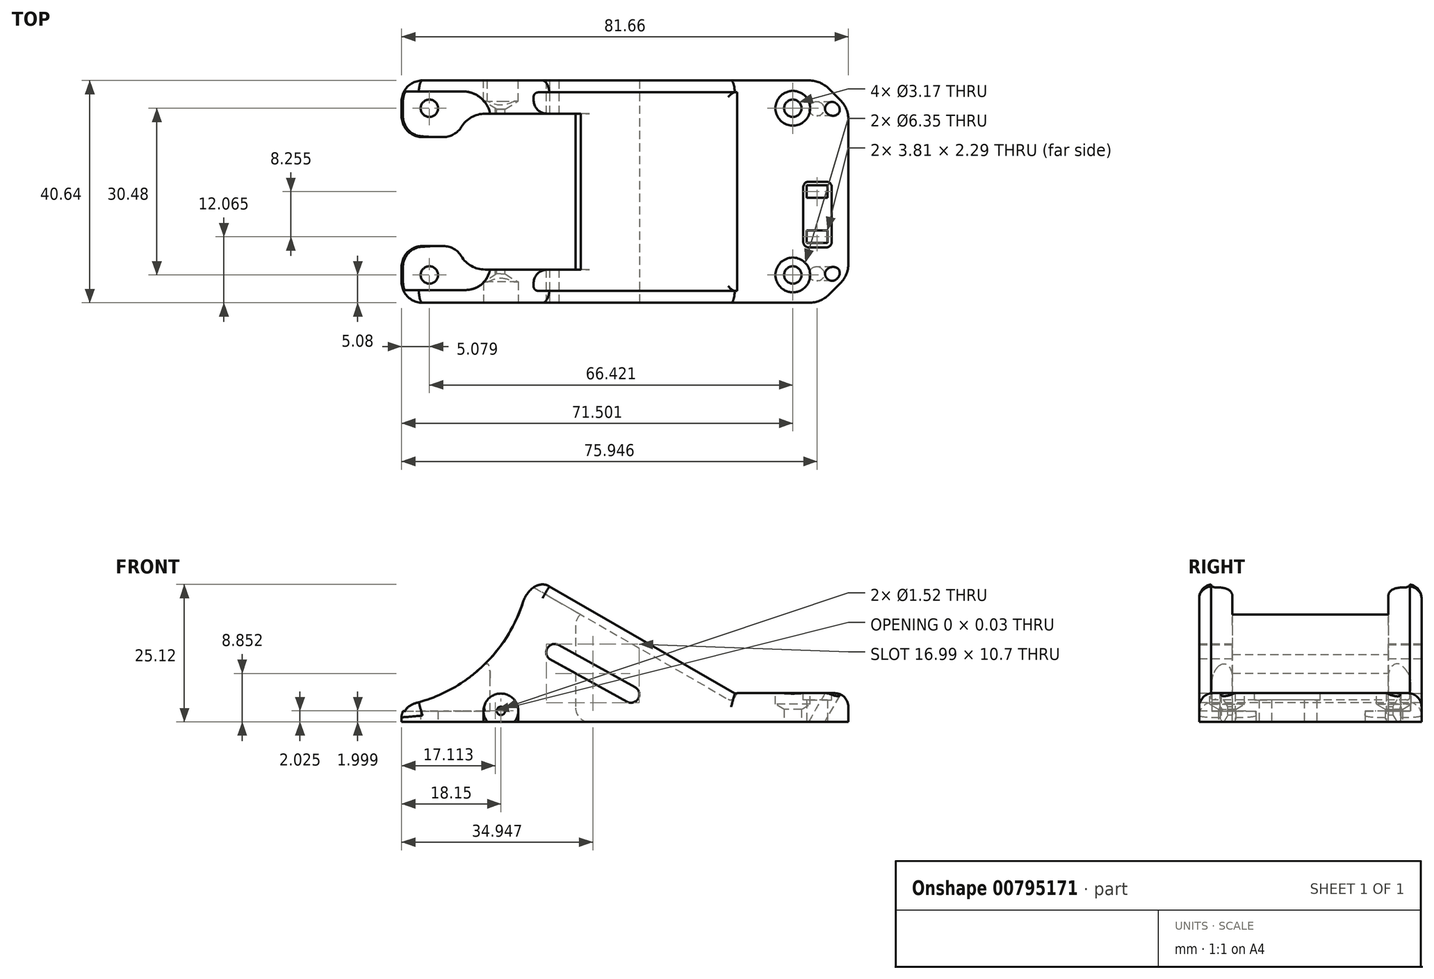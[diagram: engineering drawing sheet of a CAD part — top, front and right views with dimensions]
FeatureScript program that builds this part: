
annotation { "Feature Type Name" : "Feature", "Feature Type Description" : "" }
export const myFeature = defineFeature(function(context is Context, id is Id, definition is map)
    precondition{}
    {
        {
            var Q0;
            Q0=qCreatedBy(makeId("Top.planeOp"),FACE);
            var sketch = newSketch(context, id + "F0", { "sketchPlane" : qUnion([Q0])});
            skPoint(sketch, "E0.middle", {"position": v(0, 0) * mm});
            skCircle(sketch, "E1", {"center": v(-33.21, 15.24) * mm, "radius": 1.59 * mm});
            skCircle(sketch, "E2", {"center": v(-33.21, -15.24) * mm, "radius": 1.59 * mm});
            skCircle(sketch, "E3", {"center": v(33.21, 15.24) * mm, "radius": 1.59 * mm});
            skCircle(sketch, "E4", {"center": v(33.21, -15.24) * mm, "radius": 1.59 * mm});
            skLineSegment(sketch, "E5.bottom", {"start": v(-38.3, 20.32) * mm, "end": v(43.37, 20.32) * mm});
            skLineSegment(sketch, "E5.top", {"start": v(-38.3, -20.32) * mm, "end": v(43.37, -20.32) * mm});
            skLineSegment(sketch, "E5.left", {"start": v(-38.3, 20.32) * mm, "end": v(-38.3, 9.98) * mm});
            skLineSegment(sketch, "E5.right", {"start": v(43.37, 20.32) * mm, "end": v(43.37, -20.32) * mm});
            skLineSegment(sketch, "E6.bottom", {"start": v(-38.3, 9.98) * mm, "end": v(-26.81, 9.98) * mm});
            skLineSegment(sketch, "E6.top", {"start": v(-38.3, -9.96) * mm, "end": v(-26.82, -9.96) * mm});
            skLineSegment(sketch, "E7.left", {"start": v(-26.82, 14.25) * mm, "end": v(-26.82, 9.98) * mm});
            skLineSegment(sketch, "E7.right", {"start": v(-6.5, 14.25) * mm, "end": v(-6.5, -14.25) * mm});
            skLineSegment(sketch, "E8.trimOffspring", {"start": v(-38.3, -9.96) * mm, "end": v(-38.3, -20.32) * mm});
            skLineSegment(sketch, "E9.trimOffspring", {"start": v(-26.82, -9.96) * mm, "end": v(-26.82, -14.25) * mm});
            skLineSegment(sketch, "E10.trimOffspring", {"start": v(-26.82, 14.25) * mm, "end": v(-6.5, 14.25) * mm});
            skLineSegment(sketch, "E11.trimOffspring", {"start": v(-26.82, -14.25) * mm, "end": v(-6.5, -14.25) * mm});
            skLineSegment(sketch, "E12.bottom", {"start": v(39.56, -1.14) * mm, "end": v(35.75, -1.14) * mm});
            skLineSegment(sketch, "E12.top", {"start": v(39.56, 1.14) * mm, "end": v(35.75, 1.14) * mm});
            skLineSegment(sketch, "E12.left", {"start": v(39.56, -1.14) * mm, "end": v(39.56, 1.14) * mm});
            skLineSegment(sketch, "E12.right", {"start": v(35.75, -1.14) * mm, "end": v(35.75, 1.14) * mm});
            skPoint(sketch, "E12.middle", {"position": v(37.66, 0) * mm});
            skLineSegment(sketch, "E13.bottom", {"start": v(35.75, -7.11) * mm, "end": v(39.56, -7.11) * mm});
            skLineSegment(sketch, "E13.top", {"start": v(35.75, -9.4) * mm, "end": v(39.56, -9.4) * mm});
            skLineSegment(sketch, "E13.left", {"start": v(35.75, -7.11) * mm, "end": v(35.75, -9.4) * mm});
            skLineSegment(sketch, "E13.right", {"start": v(39.56, -7.11) * mm, "end": v(39.56, -9.4) * mm});
            skSolve(sketch);
        }
        {
            var Q0;
            Q0=makeQuery(id+"F0.imprint","IMPRINT",FACE,{"disambiguationData":[TD([[makeQuery(id+"F0.imprint","IMPRINT",EDGE,{"derivedFrom":sQuery(id+"F0.wireOp",EDGE,"E1")}),-1.0]])]});
            extrude(context, id + "F1", {"entities" : qUnion([Q0]), "depth" : 25.4 * mm, "offsetDistance" : 25.4 * mm});
        }
        {
            var Q0;
            Q0=qCreatedBy(makeId("Front.planeOp"),FACE);
            var sketch = newSketch(context, id + "F2", { "sketchPlane" : qUnion([Q0])});
            skLineSegment(sketch, "E14", {"start": v(-55.93, 50.59) * mm, "end": v(22.6, 5.24) * mm});
            skLineSegment(sketch, "E15", {"start": v(22.6, 5.24) * mm, "end": v(58.36, 5.24) * mm});
            skLineSegment(sketch, "E16", {"start": v(58.36, 5.24) * mm, "end": v(58.36, 49.59) * mm});
            skLineSegment(sketch, "E17", {"start": v(58.36, 49.59) * mm, "end": v(-55.93, 50.59) * mm});
            skSolve(sketch);
        }
        {
            var Q0;
            Q0 = qSketchRegion(id + "F2", true);
            extrude(context, id + "F3", {"entities" : qUnion([Q0]), "operationType" : NewBodyOperationType.REMOVE, "endBound" : BoundingType.SYMMETRIC, "oppositeDirection" : true, "depth" : 50.8 * mm, "offsetDistance" : 25.4 * mm});
        }
        {
            var Q0;
            Q0=qCreatedBy(makeId("Front.planeOp"),FACE);
            var sketch = newSketch(context, id + "F4", { "sketchPlane" : qUnion([Q0])});
            skCircle(sketch, "E18", {"center": v(-20.14, 2) * mm, "radius": 0.76 * mm});
            skSolve(sketch);
        }
        {
            var Q0;
            Q0 = qSketchRegion(id + "F4", true);
            extrude(context, id + "F5", {"entities" : qUnion([Q0]), "operationType" : NewBodyOperationType.REMOVE, "endBound" : BoundingType.SYMMETRIC, "depth" : 76.2 * mm, "offsetDistance" : 25.4 * mm});
        }
        {
            var Q0;
            Q0=qCreatedBy(makeId("Front.planeOp"),FACE);
            var sketch = newSketch(context, id + "F6", { "sketchPlane" : qUnion([Q0])});
            skCircle(sketch, "E19", {"center": v(-42.57, 30.4) * mm, "radius": 27.81 * mm});
            skSolve(sketch);
        }
        {
            var Q0;
            Q0=makeQuery(id+"F6.imprint","IMPRINT",FACE,{"disambiguationData":[TD([[makeQuery(id+"F6.imprint","IMPRINT",EDGE,{"derivedFrom":sQuery(id+"F6.wireOp",EDGE,"E19")}),1.0]])]});
            var Q1;
            Q1=sQuery(id+"F6.wireOp",EDGE,"E19");
            extrude(context, id + "F7", {"entities" : qUnion([Q0]), "operationType" : NewBodyOperationType.REMOVE, "surfaceEntities" : qUnion([Q1]), "endBound" : BoundingType.SYMMETRIC, "oppositeDirection" : true, "depth" : 76.2 * mm, "offsetDistance" : 25.4 * mm});
        }
        {
            var Q0;
            Q0=makeQuery(id+"F3.boolean.opBoolean","COPY",FACE,{"derivedFrom":makeQuery(id+"F3.opExtrude","SWEPT_FACE",FACE,{"disambiguationData":[OSD([sQuery(id+"F2.wireOp",EDGE,"E15")])]})});
            var sketch = newSketch(context, id + "F8", { "sketchPlane" : qUnion([Q0])});
            skPoint(sketch, "E20", {"position": v(33.21, -15.24) * mm});
            skPoint(sketch, "E21", {"position": v(33.21, 15.24) * mm});
            skPoint(sketch, "E22", {"position": v(-33.28, -15.24) * mm});
            skPoint(sketch, "E23", {"position": v(-33.28, 15.24) * mm});
            skSolve(sketch);
        }
        {
            var Q0;
            Q0=sQuery(id+"F8.wireOp",VERTEX,"E21");
            var Q1;
            Q1=sQuery(id+"F8.wireOp",VERTEX,"E20");
            var Q2;
            Q2=makeQuery(id+"F1.opExtrude","SWEPT_BODY",BODY,{"disambiguationData":[OSD([sQuery(id+"F0.wireOp",EDGE,"E1"),sQuery(id+"F0.wireOp",EDGE,"E2"),sQuery(id+"F0.wireOp",EDGE,"E3"),sQuery(id+"F0.wireOp",EDGE,"E4"),sQuery(id+"F0.wireOp",EDGE,"E5.bottom"),sQuery(id+"F0.wireOp",EDGE,"E5.top"),sQuery(id+"F0.wireOp",EDGE,"E5.left"),sQuery(id+"F0.wireOp",EDGE,"E5.right"),sQuery(id+"F0.wireOp",EDGE,"E6.bottom"),sQuery(id+"F0.wireOp",EDGE,"E6.top"),sQuery(id+"F0.wireOp",EDGE,"E7.left"),sQuery(id+"F0.wireOp",EDGE,"E7.right"),sQuery(id+"F0.wireOp",EDGE,"E8.trimOffspring"),sQuery(id+"F0.wireOp",EDGE,"E9.trimOffspring"),sQuery(id+"F0.wireOp",EDGE,"E10.trimOffspring"),sQuery(id+"F0.wireOp",EDGE,"E11.trimOffspring"),sQuery(id+"F0.wireOp",EDGE,"E12.bottom"),sQuery(id+"F0.wireOp",EDGE,"E12.top"),sQuery(id+"F0.wireOp",EDGE,"E12.left"),sQuery(id+"F0.wireOp",EDGE,"E12.right"),sQuery(id+"F0.wireOp",EDGE,"E13.bottom"),sQuery(id+"F0.wireOp",EDGE,"E13.top"),sQuery(id+"F0.wireOp",EDGE,"E13.left"),sQuery(id+"F0.wireOp",EDGE,"E13.right")])]});
            hole(context, id + "F9", {"style" : HoleStyle.SIMPLE, "endStyle" : HoleEndStyle.BLIND, "holeDiameter" : 6.35 * mm, "majorDiameter" : 6.35 * mm, "holeDepth" : 2.03 * mm, "isTappedThrough" : true, "tappedDepth" : 12.7 * mm, "tapClearance" : 3, "locations" : qUnion([Q0, Q1]), "scope" : qUnion([Q2])});
        }
        {
            var Q0;
            Q0=makeQuery(id+"F1.opExtrude","SWEPT_FACE",FACE,{"disambiguationData":[OSD([sQuery(id+"F0.wireOp",EDGE,"E5.top")])]});
            var sketch = newSketch(context, id + "F10", { "sketchPlane" : qUnion([Q0])});
            skPoint(sketch, "E24", {"position": v(-20.14, 2) * mm});
            skSolve(sketch);
        }
        {
            var Q0;
            Q0=sQuery(id+"F10.wireOp",VERTEX,"E24");
            var Q1;
            Q1=makeQuery(id+"F1.opExtrude","SWEPT_BODY",BODY,{"disambiguationData":[OSD([sQuery(id+"F0.wireOp",EDGE,"E1"),sQuery(id+"F0.wireOp",EDGE,"E2"),sQuery(id+"F0.wireOp",EDGE,"E3"),sQuery(id+"F0.wireOp",EDGE,"E4"),sQuery(id+"F0.wireOp",EDGE,"E5.bottom"),sQuery(id+"F0.wireOp",EDGE,"E5.top"),sQuery(id+"F0.wireOp",EDGE,"E5.left"),sQuery(id+"F0.wireOp",EDGE,"E5.right"),sQuery(id+"F0.wireOp",EDGE,"E6.bottom"),sQuery(id+"F0.wireOp",EDGE,"E6.top"),sQuery(id+"F0.wireOp",EDGE,"E7.left"),sQuery(id+"F0.wireOp",EDGE,"E7.right"),sQuery(id+"F0.wireOp",EDGE,"E8.trimOffspring"),sQuery(id+"F0.wireOp",EDGE,"E9.trimOffspring"),sQuery(id+"F0.wireOp",EDGE,"E10.trimOffspring"),sQuery(id+"F0.wireOp",EDGE,"E11.trimOffspring"),sQuery(id+"F0.wireOp",EDGE,"E12.bottom"),sQuery(id+"F0.wireOp",EDGE,"E12.top"),sQuery(id+"F0.wireOp",EDGE,"E12.left"),sQuery(id+"F0.wireOp",EDGE,"E12.right"),sQuery(id+"F0.wireOp",EDGE,"E13.bottom"),sQuery(id+"F0.wireOp",EDGE,"E13.top"),sQuery(id+"F0.wireOp",EDGE,"E13.left"),sQuery(id+"F0.wireOp",EDGE,"E13.right")])]});
            hole(context, id + "F11", {"style" : HoleStyle.SIMPLE, "endStyle" : HoleEndStyle.BLIND, "holeDiameter" : 6.35 * mm, "majorDiameter" : 6.35 * mm, "holeDepth" : 3.8 * mm, "isTappedThrough" : true, "tappedDepth" : 12.7 * mm, "tapClearance" : 3, "locations" : qUnion([Q0]), "scope" : qUnion([Q1])});
        }
        {
            var Q0;
            Q0=makeQuery(id+"F1.opExtrude","SWEPT_FACE",FACE,{"disambiguationData":[OSD([sQuery(id+"F0.wireOp",EDGE,"E5.bottom")])]});
            var sketch = newSketch(context, id + "F12", { "sketchPlane" : qUnion([Q0])});
            skPoint(sketch, "E25", {"position": v(20.14, 2) * mm});
            skSolve(sketch);
        }
        {
            var Q0;
            Q0=sQuery(id+"F12.wireOp",VERTEX,"E25");
            var Q1;
            Q1=makeQuery(id+"F1.opExtrude","SWEPT_BODY",BODY,{"disambiguationData":[OSD([sQuery(id+"F0.wireOp",EDGE,"E1"),sQuery(id+"F0.wireOp",EDGE,"E2"),sQuery(id+"F0.wireOp",EDGE,"E3"),sQuery(id+"F0.wireOp",EDGE,"E4"),sQuery(id+"F0.wireOp",EDGE,"E5.bottom"),sQuery(id+"F0.wireOp",EDGE,"E5.top"),sQuery(id+"F0.wireOp",EDGE,"E5.left"),sQuery(id+"F0.wireOp",EDGE,"E5.right"),sQuery(id+"F0.wireOp",EDGE,"E6.bottom"),sQuery(id+"F0.wireOp",EDGE,"E6.top"),sQuery(id+"F0.wireOp",EDGE,"E7.left"),sQuery(id+"F0.wireOp",EDGE,"E7.right"),sQuery(id+"F0.wireOp",EDGE,"E8.trimOffspring"),sQuery(id+"F0.wireOp",EDGE,"E9.trimOffspring"),sQuery(id+"F0.wireOp",EDGE,"E10.trimOffspring"),sQuery(id+"F0.wireOp",EDGE,"E11.trimOffspring"),sQuery(id+"F0.wireOp",EDGE,"E12.bottom"),sQuery(id+"F0.wireOp",EDGE,"E12.top"),sQuery(id+"F0.wireOp",EDGE,"E12.left"),sQuery(id+"F0.wireOp",EDGE,"E12.right"),sQuery(id+"F0.wireOp",EDGE,"E13.bottom"),sQuery(id+"F0.wireOp",EDGE,"E13.top"),sQuery(id+"F0.wireOp",EDGE,"E13.left"),sQuery(id+"F0.wireOp",EDGE,"E13.right")])]});
            hole(context, id + "F13", {"style" : HoleStyle.SIMPLE, "endStyle" : HoleEndStyle.BLIND, "holeDiameter" : 6.35 * mm, "majorDiameter" : 6.35 * mm, "holeDepth" : 3.8 * mm, "isTappedThrough" : true, "tappedDepth" : 12.7 * mm, "tapClearance" : 3, "locations" : qUnion([Q0]), "scope" : qUnion([Q1])});
        }
        {
            var Q0;
            Q0=makeQuery(id+"F3.boolean.opBoolean","COPY",FACE,{"derivedFrom":makeQuery(id+"F3.opExtrude","SWEPT_FACE",FACE,{"disambiguationData":[OSD([sQuery(id+"F2.wireOp",EDGE,"E15")])]})});
            var sketch = newSketch(context, id + "F14", { "sketchPlane" : qUnion([Q0])});
            skLineSegment(sketch, "E26.bottom", {"start": v(-39.7, 18.32) * mm, "end": v(-22.1, 18.32) * mm});
            skLineSegment(sketch, "E26.top", {"start": v(-39.7, -18.01) * mm, "end": v(-22.1, -18.01) * mm});
            skLineSegment(sketch, "E26.left", {"start": v(-39.7, 18.32) * mm, "end": v(-39.7, -18.01) * mm});
            skLineSegment(sketch, "E26.right", {"start": v(-22.1, 18.32) * mm, "end": v(-22.1, -18.01) * mm});
            skSolve(sketch);
        }
        {
            var Q0;
            Q0=makeQuery(id+"F14.imprint","IMPRINT",FACE,{"disambiguationData":[TD([[makeQuery(id+"F14.imprint","IMPRINT",EDGE,{"derivedFrom":sQuery(id+"F14.wireOp",EDGE,"E26.bottom")}),-1.0]])]});
            extrude(context, id + "F15", {"entities" : qUnion([Q0]), "operationType" : NewBodyOperationType.REMOVE, "oppositeDirection" : true, "depth" : 3.3 * mm, "offsetDistance" : 25.4 * mm, "hasSecondDirection" : true, "secondDirectionOppositeDirection" : false, "secondDirectionDepth" : 25.4 * mm});
        }
        {
            var Q0;
            Q0=makeQuery(id+"F1.opExtrude","SWEPT_EDGE",EDGE,{"disambiguationData":[OSD([sQuery(id+"F0.wireOp",EDGE,"E5.top"),sQuery(id+"F0.wireOp",EDGE,"E8.trimOffspring")])]});
            var Q1;
            Q1=makeQuery(id+"F1.opExtrude","SWEPT_EDGE",EDGE,{"disambiguationData":[OSD([sQuery(id+"F0.wireOp",EDGE,"E5.bottom"),sQuery(id+"F0.wireOp",EDGE,"E5.left")])]});
            var Q2;
            Q2=makeQuery(id+"F1.opExtrude","SWEPT_EDGE",EDGE,{"disambiguationData":[OSD([sQuery(id+"F0.wireOp",EDGE,"E5.left"),sQuery(id+"F0.wireOp",EDGE,"E6.bottom")])]});
            var Q3;
            Q3=makeQuery(id+"F1.opExtrude","SWEPT_EDGE",EDGE,{"disambiguationData":[OSD([sQuery(id+"F0.wireOp",EDGE,"E6.top"),sQuery(id+"F0.wireOp",EDGE,"E8.trimOffspring")])]});
            var Q4;
            Q4=makeQuery(id+"F1.opExtrude","SWEPT_EDGE",EDGE,{"disambiguationData":[OSD([sQuery(id+"F0.wireOp",EDGE,"E6.bottom"),sQuery(id+"F0.wireOp",EDGE,"E7.left")])]});
            var Q5;
            Q5=makeQuery(id+"F1.opExtrude","SWEPT_EDGE",EDGE,{"disambiguationData":[OSD([sQuery(id+"F0.wireOp",EDGE,"E6.top"),sQuery(id+"F0.wireOp",EDGE,"E9.trimOffspring")])]});
            fillet(context, id + "F16", {"entities" : qUnion([Q0, Q1, Q2, Q3, Q4, Q5]), "radius" : 3.8 * mm, "tangentPropagation" : true, "allowEdgeOverflow" : false});
        }
        {
            var Q0;
            Q0=makeQuery(id+"F1.opExtrude","SWEPT_EDGE",EDGE,{"disambiguationData":[OSD([sQuery(id+"F0.wireOp",EDGE,"E5.top"),sQuery(id+"F0.wireOp",EDGE,"E5.right")])]});
            var Q1;
            Q1=makeQuery(id+"F1.opExtrude","SWEPT_EDGE",EDGE,{"disambiguationData":[OSD([sQuery(id+"F0.wireOp",EDGE,"E5.bottom"),sQuery(id+"F0.wireOp",EDGE,"E5.right")])]});
            chamfer(context, id + "F17", {"entities" : qUnion([Q0, Q1]), "width" : 5.08 * mm, "tangentPropagation" : true});
        }
        {
            var Q0;
            {var subQ0=sQuery(id+"F0.wireOp",EDGE,"E5.top");Q0=makeQuery(id+"F17.opChamfer","BLEND_EDGE",EDGE,{"blendedFrom":[makeQuery(id+"F1.opExtrude","SWEPT_EDGE",EDGE,{"disambiguationData":[OSD([subQ0,sQuery(id+"F0.wireOp",EDGE,"E5.right")])]}),makeQuery(id+"F1.opExtrude","SWEPT_FACE",FACE,{"disambiguationData":[OSD([subQ0])]})],"blendedInto":[makeQuery(id+"F1.opExtrude","SWEPT_FACE",FACE,{"disambiguationData":[OSD([subQ0])]})]});}
            var Q1;
            {var subQ0=sQuery(id+"F0.wireOp",EDGE,"E5.right");Q1=makeQuery(id+"F17.opChamfer","BLEND_EDGE",EDGE,{"blendedFrom":[makeQuery(id+"F1.opExtrude","SWEPT_EDGE",EDGE,{"disambiguationData":[OSD([sQuery(id+"F0.wireOp",EDGE,"E5.top"),subQ0])]}),makeQuery(id+"F1.opExtrude","SWEPT_FACE",FACE,{"disambiguationData":[OSD([subQ0])]})],"blendedInto":[makeQuery(id+"F1.opExtrude","SWEPT_FACE",FACE,{"disambiguationData":[OSD([subQ0])]})]});}
            var Q2;
            {var subQ0=sQuery(id+"F0.wireOp",EDGE,"E5.right");Q2=makeQuery(id+"F17.opChamfer","BLEND_EDGE",EDGE,{"blendedFrom":[makeQuery(id+"F1.opExtrude","SWEPT_EDGE",EDGE,{"disambiguationData":[OSD([sQuery(id+"F0.wireOp",EDGE,"E5.bottom"),subQ0])]}),makeQuery(id+"F1.opExtrude","SWEPT_FACE",FACE,{"disambiguationData":[OSD([subQ0])]})],"blendedInto":[makeQuery(id+"F1.opExtrude","SWEPT_FACE",FACE,{"disambiguationData":[OSD([subQ0])]})]});}
            var Q3;
            {var subQ0=sQuery(id+"F0.wireOp",EDGE,"E5.bottom");Q3=makeQuery(id+"F17.opChamfer","BLEND_EDGE",EDGE,{"blendedFrom":[makeQuery(id+"F1.opExtrude","SWEPT_EDGE",EDGE,{"disambiguationData":[OSD([subQ0,sQuery(id+"F0.wireOp",EDGE,"E5.right")])]}),makeQuery(id+"F1.opExtrude","SWEPT_FACE",FACE,{"disambiguationData":[OSD([subQ0])]})],"blendedInto":[makeQuery(id+"F1.opExtrude","SWEPT_FACE",FACE,{"disambiguationData":[OSD([subQ0])]})]});}
            var Q4;
            {var subQ0=sQuery(id+"F0.wireOp",EDGE,"E5.left");var subQ1=sQuery(id+"F0.wireOp",EDGE,"E5.bottom");var subQ2=sQuery(id+"F0.wireOp",EDGE,"E6.bottom");var subQ3=sQuery(id+"F0.wireOp",EDGE,"E1");var subQ4=sQuery(id+"F0.wireOp",EDGE,"E7.left");var subQ5=sQuery(id+"F0.wireOp",EDGE,"E10.trimOffspring");Q4=makeQuery(id+"F7.boolean.opBoolean","INTERSECT",EDGE,{"derivedFrom":[makeQuery(id+"F3.boolean.opBoolean","SPLIT",FACE,{"disambiguationData":[TD([makeQuery(id+"F1.opExtrude","SWEPT_FACE",FACE,{"disambiguationData":[OSD([subQ3])]})])],"derivedFrom":makeQuery(id+"F1.opExtrude","CAP_FACE",FACE,{"disambiguationData":[OSD([subQ3,sQuery(id+"F0.wireOp",EDGE,"E2"),sQuery(id+"F0.wireOp",EDGE,"E3"),sQuery(id+"F0.wireOp",EDGE,"E4"),subQ1,sQuery(id+"F0.wireOp",EDGE,"E5.top"),subQ0,sQuery(id+"F0.wireOp",EDGE,"E5.right"),subQ2,sQuery(id+"F0.wireOp",EDGE,"E6.top"),subQ4,sQuery(id+"F0.wireOp",EDGE,"E7.right"),sQuery(id+"F0.wireOp",EDGE,"E8.trimOffspring"),sQuery(id+"F0.wireOp",EDGE,"E9.trimOffspring"),subQ5,sQuery(id+"F0.wireOp",EDGE,"E11.trimOffspring"),sQuery(id+"F0.wireOp",EDGE,"E12.bottom"),sQuery(id+"F0.wireOp",EDGE,"E12.top"),sQuery(id+"F0.wireOp",EDGE,"E12.left"),sQuery(id+"F0.wireOp",EDGE,"E12.right"),sQuery(id+"F0.wireOp",EDGE,"E13.bottom"),sQuery(id+"F0.wireOp",EDGE,"E13.top"),sQuery(id+"F0.wireOp",EDGE,"E13.left"),sQuery(id+"F0.wireOp",EDGE,"E13.right")])],"isStart":false})}),makeQuery(id+"F7.opExtrude","SWEPT_FACE",FACE,{"disambiguationData":[OSD([sQuery(id+"F6.wireOp",EDGE,"E19")])]})]});}
            var Q5;
            {var subQ0=sQuery(id+"F0.wireOp",EDGE,"E8.trimOffspring");var subQ1=sQuery(id+"F0.wireOp",EDGE,"E2");var subQ2=sQuery(id+"F0.wireOp",EDGE,"E6.top");var subQ3=sQuery(id+"F0.wireOp",EDGE,"E5.top");var subQ4=sQuery(id+"F0.wireOp",EDGE,"E9.trimOffspring");var subQ5=sQuery(id+"F0.wireOp",EDGE,"E11.trimOffspring");Q5=makeQuery(id+"F7.boolean.opBoolean","INTERSECT",EDGE,{"derivedFrom":[makeQuery(id+"F3.boolean.opBoolean","SPLIT",FACE,{"disambiguationData":[TD([makeQuery(id+"F1.opExtrude","SWEPT_FACE",FACE,{"disambiguationData":[OSD([subQ1])]})])],"derivedFrom":makeQuery(id+"F1.opExtrude","CAP_FACE",FACE,{"disambiguationData":[OSD([sQuery(id+"F0.wireOp",EDGE,"E1"),subQ1,sQuery(id+"F0.wireOp",EDGE,"E3"),sQuery(id+"F0.wireOp",EDGE,"E4"),sQuery(id+"F0.wireOp",EDGE,"E5.bottom"),subQ3,sQuery(id+"F0.wireOp",EDGE,"E5.left"),sQuery(id+"F0.wireOp",EDGE,"E5.right"),sQuery(id+"F0.wireOp",EDGE,"E6.bottom"),subQ2,sQuery(id+"F0.wireOp",EDGE,"E7.left"),sQuery(id+"F0.wireOp",EDGE,"E7.right"),subQ0,subQ4,sQuery(id+"F0.wireOp",EDGE,"E10.trimOffspring"),subQ5,sQuery(id+"F0.wireOp",EDGE,"E12.bottom"),sQuery(id+"F0.wireOp",EDGE,"E12.top"),sQuery(id+"F0.wireOp",EDGE,"E12.left"),sQuery(id+"F0.wireOp",EDGE,"E12.right"),sQuery(id+"F0.wireOp",EDGE,"E13.bottom"),sQuery(id+"F0.wireOp",EDGE,"E13.top"),sQuery(id+"F0.wireOp",EDGE,"E13.left"),sQuery(id+"F0.wireOp",EDGE,"E13.right")])],"isStart":false})}),makeQuery(id+"F7.opExtrude","SWEPT_FACE",FACE,{"disambiguationData":[OSD([sQuery(id+"F6.wireOp",EDGE,"E19")])]})]});}
            fillet(context, id + "F18", {"entities" : qUnion([Q0, Q1, Q2, Q3, Q4, Q5]), "radius" : 5.08 * mm, "tangentPropagation" : true, "allowEdgeOverflow" : false});
        }
        {
            var Q0;
            Q0=makeQuery(id+"F3.boolean.opBoolean","INTERSECT",EDGE,{"derivedFrom":[makeQuery(id+"F1.opExtrude","SWEPT_FACE",FACE,{"disambiguationData":[OSD([sQuery(id+"F0.wireOp",EDGE,"E5.top")])]}),makeQuery(id+"F3.opExtrude","SWEPT_FACE",FACE,{"disambiguationData":[OSD([sQuery(id+"F2.wireOp",EDGE,"E14")])]})]});
            var Q1;
            Q1=makeQuery(id+"F3.boolean.opBoolean","INTERSECT",EDGE,{"derivedFrom":[makeQuery(id+"F1.opExtrude","SWEPT_FACE",FACE,{"disambiguationData":[OSD([sQuery(id+"F0.wireOp",EDGE,"E5.top")])]}),makeQuery(id+"F3.opExtrude","SWEPT_FACE",FACE,{"disambiguationData":[OSD([sQuery(id+"F2.wireOp",EDGE,"E15")])]})]});
            var Q2;
            Q2=makeQuery(id+"F3.boolean.opBoolean","INTERSECT",EDGE,{"derivedFrom":[makeQuery(id+"F1.opExtrude","SWEPT_FACE",FACE,{"disambiguationData":[OSD([sQuery(id+"F0.wireOp",EDGE,"E5.bottom")])]}),makeQuery(id+"F3.opExtrude","SWEPT_FACE",FACE,{"disambiguationData":[OSD([sQuery(id+"F2.wireOp",EDGE,"E14")])]})]});
            var Q3;
            {var subQ0=makeQuery(id+"F3.opExtrude","SWEPT_FACE",FACE,{"disambiguationData":[OSD([sQuery(id+"F2.wireOp",EDGE,"E14")])]});var subQ1=sQuery(id+"F0.wireOp",EDGE,"E8.trimOffspring");var subQ2=sQuery(id+"F0.wireOp",EDGE,"E2");var subQ3=sQuery(id+"F0.wireOp",EDGE,"E6.top");var subQ4=sQuery(id+"F0.wireOp",EDGE,"E5.top");var subQ5=sQuery(id+"F0.wireOp",EDGE,"E9.trimOffspring");var subQ6=sQuery(id+"F0.wireOp",EDGE,"E11.trimOffspring");Q3=makeQuery(id+"F18.opFillet","BLEND_EDGE",EDGE,{"blendedFrom":[makeQuery(id+"F7.boolean.opBoolean","INTERSECT",EDGE,{"derivedFrom":[makeQuery(id+"F3.boolean.opBoolean","SPLIT",FACE,{"disambiguationData":[TD([makeQuery(id+"F1.opExtrude","SWEPT_FACE",FACE,{"disambiguationData":[OSD([subQ2])]})])],"derivedFrom":makeQuery(id+"F1.opExtrude","CAP_FACE",FACE,{"disambiguationData":[OSD([sQuery(id+"F0.wireOp",EDGE,"E1"),subQ2,sQuery(id+"F0.wireOp",EDGE,"E3"),sQuery(id+"F0.wireOp",EDGE,"E4"),sQuery(id+"F0.wireOp",EDGE,"E5.bottom"),subQ4,sQuery(id+"F0.wireOp",EDGE,"E5.left"),sQuery(id+"F0.wireOp",EDGE,"E5.right"),sQuery(id+"F0.wireOp",EDGE,"E6.bottom"),subQ3,sQuery(id+"F0.wireOp",EDGE,"E7.left"),sQuery(id+"F0.wireOp",EDGE,"E7.right"),subQ1,subQ5,sQuery(id+"F0.wireOp",EDGE,"E10.trimOffspring"),subQ6,sQuery(id+"F0.wireOp",EDGE,"E12.bottom"),sQuery(id+"F0.wireOp",EDGE,"E12.top"),sQuery(id+"F0.wireOp",EDGE,"E12.left"),sQuery(id+"F0.wireOp",EDGE,"E12.right"),sQuery(id+"F0.wireOp",EDGE,"E13.bottom"),sQuery(id+"F0.wireOp",EDGE,"E13.top"),sQuery(id+"F0.wireOp",EDGE,"E13.left"),sQuery(id+"F0.wireOp",EDGE,"E13.right")])],"isStart":false})}),makeQuery(id+"F7.opExtrude","SWEPT_FACE",FACE,{"disambiguationData":[OSD([sQuery(id+"F6.wireOp",EDGE,"E19")])]})]}),makeQuery(id+"F3.boolean.opBoolean","COPY",FACE,{"derivedFrom":subQ0})],"blendedInto":[makeQuery(id+"F3.boolean.opBoolean","COPY",FACE,{"derivedFrom":subQ0})]});}
            var Q4;
            {var subQ0=makeQuery(id+"F3.opExtrude","SWEPT_FACE",FACE,{"disambiguationData":[OSD([sQuery(id+"F2.wireOp",EDGE,"E14")])]});var subQ1=sQuery(id+"F0.wireOp",EDGE,"E5.left");var subQ2=sQuery(id+"F0.wireOp",EDGE,"E5.bottom");var subQ3=sQuery(id+"F0.wireOp",EDGE,"E6.bottom");var subQ4=sQuery(id+"F0.wireOp",EDGE,"E1");var subQ5=sQuery(id+"F0.wireOp",EDGE,"E7.left");var subQ6=sQuery(id+"F0.wireOp",EDGE,"E10.trimOffspring");Q4=makeQuery(id+"F18.opFillet","BLEND_EDGE",EDGE,{"blendedFrom":[makeQuery(id+"F7.boolean.opBoolean","INTERSECT",EDGE,{"derivedFrom":[makeQuery(id+"F3.boolean.opBoolean","SPLIT",FACE,{"disambiguationData":[TD([makeQuery(id+"F1.opExtrude","SWEPT_FACE",FACE,{"disambiguationData":[OSD([subQ4])]})])],"derivedFrom":makeQuery(id+"F1.opExtrude","CAP_FACE",FACE,{"disambiguationData":[OSD([subQ4,sQuery(id+"F0.wireOp",EDGE,"E2"),sQuery(id+"F0.wireOp",EDGE,"E3"),sQuery(id+"F0.wireOp",EDGE,"E4"),subQ2,sQuery(id+"F0.wireOp",EDGE,"E5.top"),subQ1,sQuery(id+"F0.wireOp",EDGE,"E5.right"),subQ3,sQuery(id+"F0.wireOp",EDGE,"E6.top"),subQ5,sQuery(id+"F0.wireOp",EDGE,"E7.right"),sQuery(id+"F0.wireOp",EDGE,"E8.trimOffspring"),sQuery(id+"F0.wireOp",EDGE,"E9.trimOffspring"),subQ6,sQuery(id+"F0.wireOp",EDGE,"E11.trimOffspring"),sQuery(id+"F0.wireOp",EDGE,"E12.bottom"),sQuery(id+"F0.wireOp",EDGE,"E12.top"),sQuery(id+"F0.wireOp",EDGE,"E12.left"),sQuery(id+"F0.wireOp",EDGE,"E12.right"),sQuery(id+"F0.wireOp",EDGE,"E13.bottom"),sQuery(id+"F0.wireOp",EDGE,"E13.top"),sQuery(id+"F0.wireOp",EDGE,"E13.left"),sQuery(id+"F0.wireOp",EDGE,"E13.right")])],"isStart":false})}),makeQuery(id+"F7.opExtrude","SWEPT_FACE",FACE,{"disambiguationData":[OSD([sQuery(id+"F6.wireOp",EDGE,"E19")])]})]}),makeQuery(id+"F3.boolean.opBoolean","COPY",FACE,{"derivedFrom":subQ0})],"blendedInto":[makeQuery(id+"F3.boolean.opBoolean","COPY",FACE,{"derivedFrom":subQ0})]});}
            var Q5;
            Q5=makeQuery(id+"F3.boolean.opBoolean","INTERSECT",EDGE,{"derivedFrom":[makeQuery(id+"F1.opExtrude","SWEPT_FACE",FACE,{"disambiguationData":[OSD([sQuery(id+"F0.wireOp",EDGE,"E7.right")])]}),makeQuery(id+"F3.opExtrude","SWEPT_FACE",FACE,{"disambiguationData":[OSD([sQuery(id+"F2.wireOp",EDGE,"E14")])]})]});
            var Q6;
            Q6=makeQuery(id+"F1.opExtrude","CAP_EDGE",EDGE,{"disambiguationData":[OSD([sQuery(id+"F0.wireOp",EDGE,"E7.right")])],"isStart":true});
            var Q7;
            Q7=makeQuery(id+"F3.boolean.opBoolean","INTERSECT",EDGE,{"derivedFrom":[makeQuery(id+"F1.opExtrude","SWEPT_FACE",FACE,{"disambiguationData":[OSD([sQuery(id+"F0.wireOp",EDGE,"E5.bottom")])]}),makeQuery(id+"F3.opExtrude","SWEPT_FACE",FACE,{"disambiguationData":[OSD([sQuery(id+"F2.wireOp",EDGE,"E15")])]})]});
            var Q8;
            Q8=makeQuery(id+"F3.boolean.opBoolean","INTERSECT",EDGE,{"derivedFrom":[makeQuery(id+"F1.opExtrude","SWEPT_FACE",FACE,{"disambiguationData":[OSD([sQuery(id+"F0.wireOp",EDGE,"E5.right")])]}),makeQuery(id+"F3.opExtrude","SWEPT_FACE",FACE,{"disambiguationData":[OSD([sQuery(id+"F2.wireOp",EDGE,"E15")])]})]});
            fillet(context, id + "F19", {"entities" : qUnion([Q0, Q1, Q2, Q3, Q4, Q5, Q6, Q7, Q8]), "radius" : 2.54 * mm, "tangentPropagation" : true, "allowEdgeOverflow" : false});
        }
        {
            var Q0;
            Q0=makeQuery(id+"F3.boolean.opBoolean","COPY",FACE,{"derivedFrom":makeQuery(id+"F3.opExtrude","SWEPT_FACE",FACE,{"disambiguationData":[OSD([sQuery(id+"F2.wireOp",EDGE,"E15")])]})});
            var sketch = newSketch(context, id + "F20", { "sketchPlane" : qUnion([Q0])});
            skLineSegment(sketch, "E27.bottom", {"start": v(35.12, 1.83) * mm, "end": v(40.32, 1.83) * mm});
            skLineSegment(sketch, "E27.top", {"start": v(35.12, -10.2) * mm, "end": v(40.32, -10.2) * mm});
            skLineSegment(sketch, "E27.left", {"start": v(35.12, 1.83) * mm, "end": v(35.12, -10.2) * mm});
            skLineSegment(sketch, "E27.right", {"start": v(40.32, 1.83) * mm, "end": v(40.32, -10.2) * mm});
            skSolve(sketch);
        }
        {
            var Q0;
            Q0=makeQuery(id+"F20.imprint","IMPRINT",FACE,{"disambiguationData":[TD([[makeQuery(id+"F20.imprint","IMPRINT",EDGE,{"derivedFrom":sQuery(id+"F20.wireOp",EDGE,"E27.bottom")}),-1.0]])]});
            extrude(context, id + "F21", {"entities" : qUnion([Q0]), "operationType" : NewBodyOperationType.REMOVE, "oppositeDirection" : true, "depth" : 1.27 * mm, "offsetDistance" : 25.4 * mm});
        }
        {
            var Q0;
            Q0=makeQuery(id+"F1.opExtrude","SWEPT_FACE",FACE,{"disambiguationData":[OSD([sQuery(id+"F0.wireOp",EDGE,"E5.bottom")])]});
            var sketch = newSketch(context, id + "F22", { "sketchPlane" : qUnion([Q0])});
            skLineSegment(sketch, "E28.bottom", {"start": v(16.96, 1.98) * mm, "end": v(23.3, 1.98) * mm});
            skLineSegment(sketch, "E28.top", {"start": v(16.96, -1.16) * mm, "end": v(23.3, -1.16) * mm});
            skLineSegment(sketch, "E28.left", {"start": v(16.96, 1.98) * mm, "end": v(16.96, -1.16) * mm});
            skLineSegment(sketch, "E28.right", {"start": v(23.3, 1.98) * mm, "end": v(23.3, -1.16) * mm});
            skSolve(sketch);
        }
        {
            var Q0;
            {var subQ0=sQuery(id+"F22.wireOp",EDGE,"E28.left");var subQ3=makeQuery(id+"F1.opExtrude","CAP_EDGE",EDGE,{"disambiguationData":[OSD([sQuery(id+"F0.wireOp",EDGE,"E5.bottom")])],"isStart":true});var subQ4=makeQuery(id+"F22.imprint","INTERSECT",VERTEX,{"derivedFrom":[subQ3,subQ0]});Q0=makeQuery(id+"F22.imprint","IMPRINT",FACE,{"disambiguationData":[TD([[makeQuery(id+"F22.imprint","IMPRINT",EDGE,{"disambiguationData":[TD([[subQ4,1.0]])],"derivedFrom":subQ3}),-1.0]])]});}
            var Q1;
            {var subQ1=sQuery(id+"F22.wireOp",EDGE,"E28.bottom");Q1=makeQuery(id+"F22.imprint","IMPRINT",FACE,{"disambiguationData":[TD([[makeQuery(id+"F22.imprint","IMPRINT",EDGE,{"derivedFrom":subQ1}),-1.0]])]});}
            extrude(context, id + "F23", {"entities" : qUnion([Q0, Q1]), "operationType" : NewBodyOperationType.REMOVE, "oppositeDirection" : true, "depth" : 3.8 * mm, "offsetDistance" : 25.4 * mm});
        }
        {
            var Q0;
            Q0=makeQuery(id+"F1.opExtrude","SWEPT_FACE",FACE,{"disambiguationData":[OSD([sQuery(id+"F0.wireOp",EDGE,"E5.top")])]});
            var sketch = newSketch(context, id + "F24", { "sketchPlane" : qUnion([Q0])});
            skLineSegment(sketch, "E29.bottom", {"start": v(-16.97, 2.06) * mm, "end": v(-23.31, 2.06) * mm});
            skLineSegment(sketch, "E29.top", {"start": v(-16.97, -1.93) * mm, "end": v(-23.31, -1.93) * mm});
            skLineSegment(sketch, "E29.left", {"start": v(-16.97, 2.06) * mm, "end": v(-16.97, -1.93) * mm});
            skLineSegment(sketch, "E29.right", {"start": v(-23.31, 2.06) * mm, "end": v(-23.31, -1.93) * mm});
            skSolve(sketch);
        }
        {
            var Q0;
            Q0 = qSketchRegion(id + "F24", true);
            extrude(context, id + "F25", {"entities" : qUnion([Q0]), "operationType" : NewBodyOperationType.REMOVE, "oppositeDirection" : true, "depth" : 3.8 * mm, "offsetDistance" : 25.4 * mm});
        }
        {
            var Q0;
            Q0=makeQuery(id+"F1.opExtrude","SWEPT_EDGE",EDGE,{"disambiguationData":[OSD([sQuery(id+"F0.wireOp",EDGE,"E7.left"),sQuery(id+"F0.wireOp",EDGE,"E10.trimOffspring")])]});
            var Q1;
            Q1=makeQuery(id+"F1.opExtrude","SWEPT_EDGE",EDGE,{"disambiguationData":[OSD([sQuery(id+"F0.wireOp",EDGE,"E9.trimOffspring"),sQuery(id+"F0.wireOp",EDGE,"E11.trimOffspring")])]});
            fillet(context, id + "F26", {"entities" : qUnion([Q0, Q1]), "radius" : 5.08 * mm, "tangentPropagation" : true, "allowEdgeOverflow" : false});
        }
        {
            var Q0;
            Q0=qCreatedBy(makeId("Front.planeOp"),FACE);
            var sketch = newSketch(context, id + "F27", { "sketchPlane" : qUnion([Q0])});
            skLineSegment(sketch, "E30", {"start": v(-17.08, 26.25) * mm, "end": v(22.15, 3.7) * mm});
            skLineSegment(sketch, "E31", {"start": v(22.15, 3.7) * mm, "end": v(26.28, 10.86) * mm});
            skLineSegment(sketch, "E32", {"start": v(26.28, 10.86) * mm, "end": v(-11.79, 32.75) * mm});
            skLineSegment(sketch, "E33", {"start": v(-11.79, 32.75) * mm, "end": v(-17.08, 26.25) * mm});
            skSolve(sketch);
        }
        {
            var Q0;
            Q0=makeQuery(id+"F27.imprint","IMPRINT",FACE,{"disambiguationData":[TD([[makeQuery(id+"F27.imprint","IMPRINT",EDGE,{"derivedFrom":sQuery(id+"F27.wireOp",EDGE,"E30")}),1.0]])]});
            extrude(context, id + "F28", {"entities" : qUnion([Q0]), "operationType" : NewBodyOperationType.REMOVE, "endBound" : BoundingType.SYMMETRIC, "depth" : 36.32 * mm, "offsetDistance" : 25.4 * mm});
        }
        {
            var Q0;
            Q0=makeQuery(id+"F28.boolean.opBoolean","COPY",EDGE,{"derivedFrom":makeQuery(id+"F28.opExtrude","CAP_EDGE",EDGE,{"disambiguationData":[OSD([sQuery(id+"F27.wireOp",EDGE,"E30")])],"isStart":true})});
            var Q1;
            Q1=makeQuery(id+"F28.boolean.opBoolean","COPY",EDGE,{"derivedFrom":makeQuery(id+"F28.opExtrude","CAP_EDGE",EDGE,{"disambiguationData":[OSD([sQuery(id+"F27.wireOp",EDGE,"E30")])],"isStart":false})});
            var Q2;
            Q2=makeQuery(id+"F28.boolean.opBoolean","COPY",EDGE,{"derivedFrom":makeQuery(id+"F28.opExtrude","SWEPT_EDGE",EDGE,{"disambiguationData":[OSD([sQuery(id+"F27.wireOp",EDGE,"E30"),sQuery(id+"F27.wireOp",EDGE,"E31")])]})});
            fillet(context, id + "F29", {"entities" : qUnion([Q0, Q1, Q2]), "radius" : 0.89 * mm, "tangentPropagation" : true, "allowEdgeOverflow" : false});
        }
        {
            var Q0;
            Q0=qCreatedBy(makeId("Front.planeOp"),FACE);
            var sketch = newSketch(context, id + "F30", { "sketchPlane" : qUnion([Q0])});
            skArc(sketch, "E34", {"start": v(-9.54, 14) * mm, "mid": v(-11.7, 13.38) * mm, "end": v(-10.9, 11.28) * mm});
            skArc(sketch, "E35", {"start": v(2.9, 3.68) * mm, "mid": v(4.97, 4.28) * mm, "end": v(4.37, 6.35) * mm});
            skLineSegment(sketch, "E36", {"start": v(-9.54, 14) * mm, "end": v(4.37, 6.35) * mm});
            skLineSegment(sketch, "E37", {"start": v(-11.24, 11.47) * mm, "end": v(2.9, 3.68) * mm});
            skSolve(sketch);
        }
        {
            var Q0;
            {var subQ5=sQuery(id+"F30.wireOp",EDGE,"E35");Q0=makeQuery(id+"F30.imprint","IMPRINT",FACE,{"disambiguationData":[TD([[makeQuery(id+"F30.imprint","IMPRINT",EDGE,{"derivedFrom":subQ5}),1.0]])]});}
            extrude(context, id + "F31", {"entities" : qUnion([Q0]), "operationType" : NewBodyOperationType.REMOVE, "endBound" : BoundingType.SYMMETRIC, "oppositeDirection" : true, "depth" : 76.2 * mm, "offsetDistance" : 25.4 * mm});
        }
        {
            var Q0;
            Q0=makeQuery(id+"F21.boolean.opBoolean","COPY",EDGE,{"derivedFrom":makeQuery(id+"F21.opExtrude","SWEPT_EDGE",EDGE,{"disambiguationData":[OSD([sQuery(id+"F20.wireOp",EDGE,"E27.bottom"),sQuery(id+"F20.wireOp",EDGE,"E27.right")])]})});
            var Q1;
            Q1=makeQuery(id+"F21.boolean.opBoolean","COPY",EDGE,{"derivedFrom":makeQuery(id+"F21.opExtrude","SWEPT_EDGE",EDGE,{"disambiguationData":[OSD([sQuery(id+"F20.wireOp",EDGE,"E27.bottom"),sQuery(id+"F20.wireOp",EDGE,"E27.left")])]})});
            var Q2;
            Q2=makeQuery(id+"F21.boolean.opBoolean","COPY",EDGE,{"derivedFrom":makeQuery(id+"F21.opExtrude","SWEPT_EDGE",EDGE,{"disambiguationData":[OSD([sQuery(id+"F20.wireOp",EDGE,"E27.top"),sQuery(id+"F20.wireOp",EDGE,"E27.left")])]})});
            var Q3;
            Q3=makeQuery(id+"F21.boolean.opBoolean","COPY",EDGE,{"derivedFrom":makeQuery(id+"F21.opExtrude","SWEPT_EDGE",EDGE,{"disambiguationData":[OSD([sQuery(id+"F20.wireOp",EDGE,"E27.top"),sQuery(id+"F20.wireOp",EDGE,"E27.right")])]})});
            fillet(context, id + "F32", {"entities" : qUnion([Q0, Q1, Q2, Q3]), "radius" : 1.02 * mm, "tangentPropagation" : true, "allowEdgeOverflow" : false});
        }
        {
            var Q0;
            Q0=makeQuery(id+"F15.boolean.opBoolean","COPY",EDGE,{"derivedFrom":makeQuery(id+"F15.opExtrude","SWEPT_EDGE",EDGE,{"disambiguationData":[OSD([sQuery(id+"F14.wireOp",EDGE,"E26.bottom"),sQuery(id+"F14.wireOp",EDGE,"E26.right")])]})});
            fillet(context, id + "F33", {"entities" : qUnion([Q0]), "radius" : 5.08 * mm, "tangentPropagation" : true, "allowEdgeOverflow" : false});
        }
        {
            var Q0;
            Q0=qCreatedBy(makeId("Front.planeOp"),FACE);
            var sketch = newSketch(context, id + "F34", { "sketchPlane" : qUnion([Q0])});
            skArc(sketch, "E38", {"start": v(-19.15, 2.04) * mm, "mid": v(-20.18, 3.04) * mm, "end": v(-21.18, 2) * mm});
            skLineSegment(sketch, "E39.bottom", {"start": v(-19.15, 2.04) * mm, "end": v(-19.15, 2.04) * mm});
            skLineSegment(sketch, "E39.top", {"start": v(-21.18, -0.3) * mm, "end": v(-19.15, -0.3) * mm});
            skLineSegment(sketch, "E39.left", {"start": v(-21.18, 2.04) * mm, "end": v(-21.18, -0.3) * mm});
            skLineSegment(sketch, "E39.right", {"start": v(-19.15, 2.04) * mm, "end": v(-19.15, -0.3) * mm});
            skSolve(sketch);
        }
        {
            var Q0;
            {var subQ1=sQuery(id+"F34.wireOp",EDGE,"E38");Q0=makeQuery(id+"F34.imprint","IMPRINT",FACE,{"disambiguationData":[TD([[makeQuery(id+"F34.imprint","IMPRINT",EDGE,{"derivedFrom":subQ1}),1.0]])]});}
            extrude(context, id + "F35", {"entities" : qUnion([Q0]), "operationType" : NewBodyOperationType.REMOVE, "endBound" : BoundingType.SYMMETRIC, "depth" : 30.23 * mm, "offsetDistance" : 25.4 * mm});
        }
        {
            var Q0;
            Q0=makeQuery(id+"F15.boolean.opBoolean","COPY",EDGE,{"derivedFrom":makeQuery(id+"F15.opExtrude","SWEPT_EDGE",EDGE,{"disambiguationData":[OSD([sQuery(id+"F14.wireOp",EDGE,"E26.bottom"),sQuery(id+"F14.wireOp",EDGE,"E26.right")])]})});
            var Q1;
            Q1=makeQuery(id+"F15.boolean.opBoolean","COPY",EDGE,{"derivedFrom":makeQuery(id+"F15.opExtrude","SWEPT_EDGE",EDGE,{"disambiguationData":[OSD([sQuery(id+"F14.wireOp",EDGE,"E26.top"),sQuery(id+"F14.wireOp",EDGE,"E26.right")])]})});
            fillet(context, id + "F36", {"entities" : qUnion([Q0, Q1]), "radius" : 5.08 * mm, "tangentPropagation" : true, "rho" : 0.5, "crossSection" : FilletCrossSection.CONIC, "allowEdgeOverflow" : false});
        }
        {
            var Q0;
            Q0=makeQuery(id+"F28.boolean.opBoolean","COPY",FACE,{"derivedFrom":makeQuery(id+"F28.opExtrude","SWEPT_FACE",FACE,{"disambiguationData":[OSD([sQuery(id+"F27.wireOp",EDGE,"E30")])]})});
            var sketch = newSketch(context, id + "F37", { "sketchPlane" : qUnion([Q0])});
            skCircle(sketch, "E40", {"center": v(32.55, 15.14) * mm, "radius": 1.27 * mm});
            skCircle(sketch, "E41", {"center": v(32.55, -15.04) * mm, "radius": 1.27 * mm});
            skSolve(sketch);
        }
        {
            var Q0;
            Q0=makeQuery(id+"F37.imprint","IMPRINT",FACE,{"disambiguationData":[TD([[makeQuery(id+"F37.imprint","IMPRINT",EDGE,{"derivedFrom":sQuery(id+"F37.wireOp",EDGE,"E41")}),1.0]])]});
            var Q1;
            Q1=makeQuery(id+"F37.imprint","IMPRINT",FACE,{"disambiguationData":[TD([[makeQuery(id+"F37.imprint","IMPRINT",EDGE,{"derivedFrom":sQuery(id+"F37.wireOp",EDGE,"E40")}),1.0]])]});
            extrude(context, id + "F38", {"entities" : qUnion([Q0, Q1]), "operationType" : NewBodyOperationType.REMOVE, "depth" : 25.4 * mm, "offsetDistance" : 25.4 * mm});
        }
        {
            var Q0;
            Q0=makeQuery(id+"F7.boolean.opBoolean","INTERSECT",EDGE,{"derivedFrom":[makeQuery(id+"F1.opExtrude","SWEPT_FACE",FACE,{"disambiguationData":[OSD([sQuery(id+"F0.wireOp",EDGE,"E5.top")])]}),makeQuery(id+"F7.opExtrude","SWEPT_FACE",FACE,{"disambiguationData":[OSD([sQuery(id+"F6.wireOp",EDGE,"E19")])]})]});
            var Q1;
            Q1=makeQuery(id+"F7.boolean.opBoolean","INTERSECT",EDGE,{"derivedFrom":[makeQuery(id+"F1.opExtrude","SWEPT_FACE",FACE,{"disambiguationData":[OSD([sQuery(id+"F0.wireOp",EDGE,"E5.bottom")])]}),makeQuery(id+"F7.opExtrude","SWEPT_FACE",FACE,{"disambiguationData":[OSD([sQuery(id+"F6.wireOp",EDGE,"E19")])]})]});
            fillet(context, id + "F39", {"entities" : qUnion([Q0, Q1]), "radius" : 2.54 * mm, "tangentPropagation" : true, "allowEdgeOverflow" : false});
        }
        {
            var Q0;
            Q0=makeQuery(id+"F7.boolean.opBoolean","INTERSECT",EDGE,{"derivedFrom":[makeQuery(id+"F1.opExtrude","SWEPT_FACE",FACE,{"disambiguationData":[OSD([sQuery(id+"F0.wireOp",EDGE,"E10.trimOffspring")])]}),makeQuery(id+"F7.opExtrude","SWEPT_FACE",FACE,{"disambiguationData":[OSD([sQuery(id+"F6.wireOp",EDGE,"E19")])]})]});
            var Q1;
            Q1=makeQuery(id+"F7.boolean.opBoolean","INTERSECT",EDGE,{"derivedFrom":[makeQuery(id+"F1.opExtrude","SWEPT_FACE",FACE,{"disambiguationData":[OSD([sQuery(id+"F0.wireOp",EDGE,"E11.trimOffspring")])]}),makeQuery(id+"F7.opExtrude","SWEPT_FACE",FACE,{"disambiguationData":[OSD([sQuery(id+"F6.wireOp",EDGE,"E19")])]})]});
            fillet(context, id + "F40", {"entities" : qUnion([Q0, Q1]), "radius" : 2.54 * mm, "tangentPropagation" : true, "allowEdgeOverflow" : false});
        }
    });
